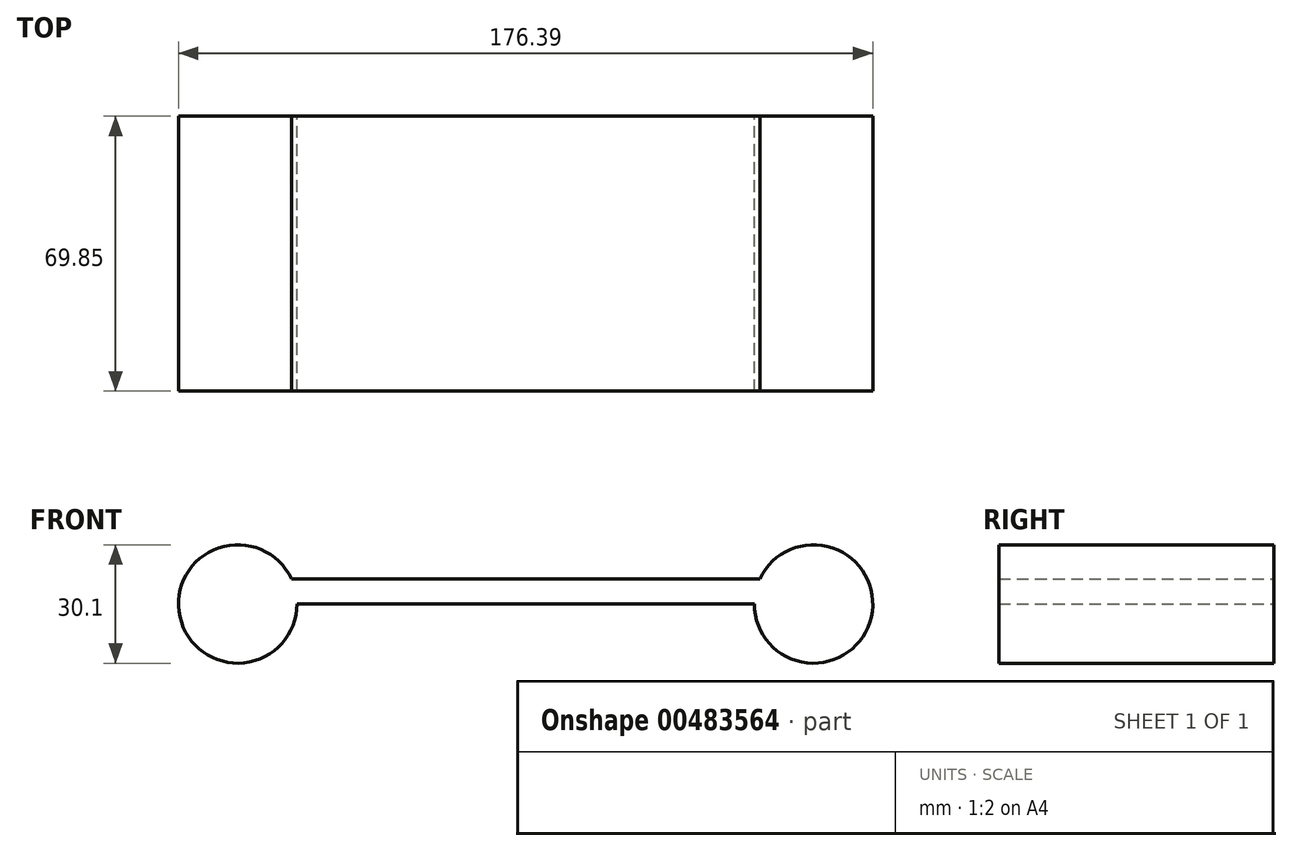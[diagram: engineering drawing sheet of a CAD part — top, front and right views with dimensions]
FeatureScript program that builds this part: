
annotation { "Feature Type Name" : "Feature", "Feature Type Description" : "" }
export const myFeature = defineFeature(function(context is Context, id is Id, definition is map)
    precondition{}
    {
        {
            var Q0;
            Q0=qCreatedBy(makeId("Front.planeOp"),FACE);
            var sketch = newSketch(context, id + "F0", { "sketchPlane" : qUnion([Q0])});
            skLineSegment(sketch, "E0", {"start": v(-88.02, 13.63) * mm, "end": v(89.78, 13.63) * mm});
            skLineSegment(sketch, "E1", {"start": v(-88.02, 13.63) * mm, "end": v(-88.02, 7.28) * mm});
            skLineSegment(sketch, "E2", {"start": v(-88.02, 7.28) * mm, "end": v(89.78, 7.28) * mm});
            skCircle(sketch, "E3", {"center": v(69.44, 7.28) * mm, "radius": 15.05 * mm});
            skCircle(sketch, "E4", {"center": v(-76.85, 7.28) * mm, "radius": 15.05 * mm});
            skSolve(sketch);
        }
        {
            var Q0;
            Q0 = qSketchRegion(id + "F0", true);
            extrude(context, id + "F1", {"entities" : qUnion([Q0]), "depth" : 69.85 * mm});
        }
    });
